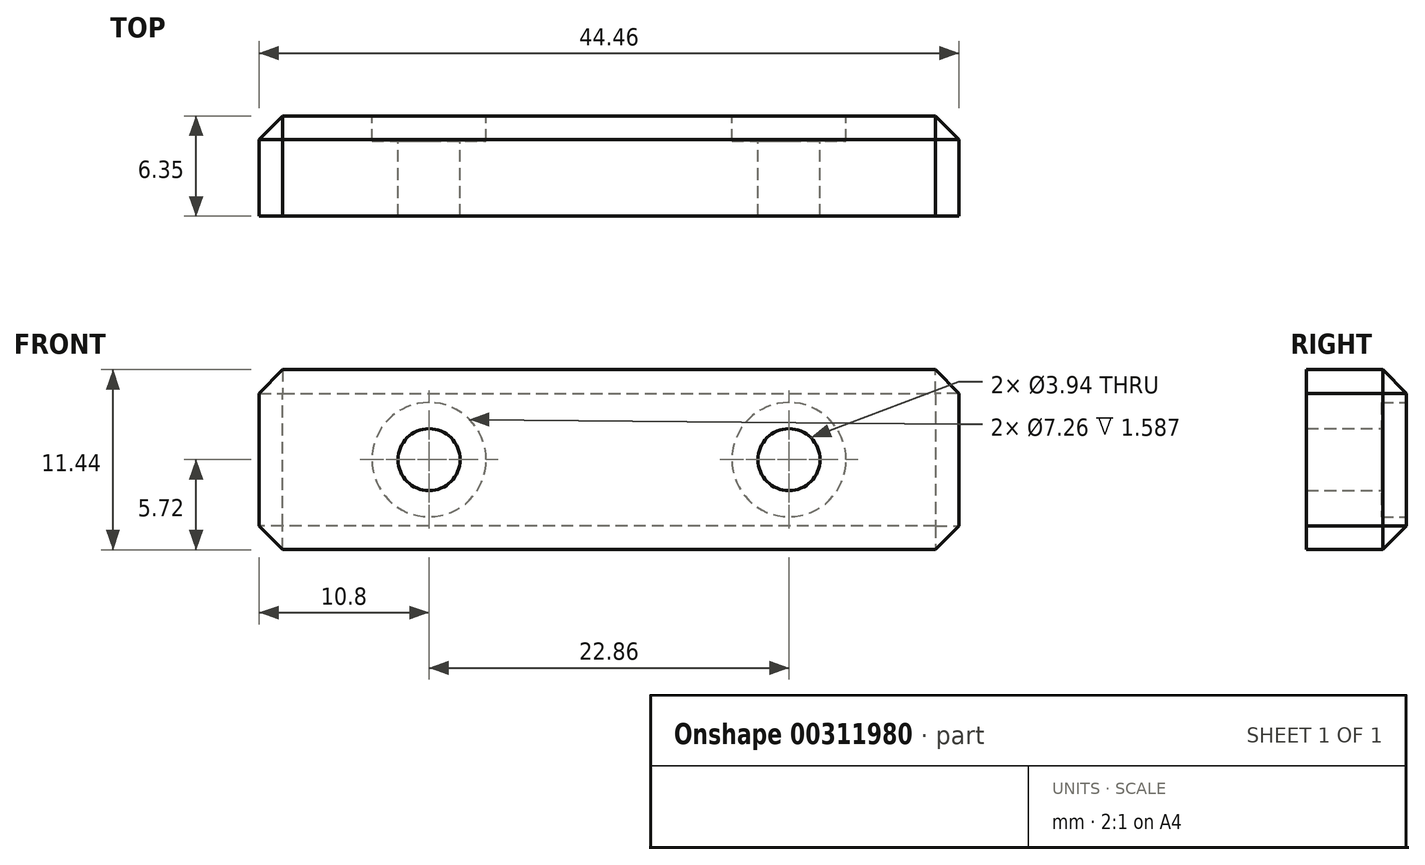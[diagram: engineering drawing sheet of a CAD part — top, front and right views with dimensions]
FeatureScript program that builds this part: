
annotation { "Feature Type Name" : "Feature", "Feature Type Description" : "" }
export const myFeature = defineFeature(function(context is Context, id is Id, definition is map)
    precondition{}
    {
        {
            var Q0;
            Q0=qCreatedBy(makeId("Front.planeOp"),FACE);
            var sketch = newSketch(context, id + "F0", { "sketchPlane" : qUnion([Q0])});
            skLineSegment(sketch, "E0.bottom", {"start": v(-22.23, 5.72) * mm, "end": v(22.23, 5.72) * mm});
            skLineSegment(sketch, "E0.top", {"start": v(-22.23, -5.71) * mm, "end": v(22.23, -5.71) * mm});
            skLineSegment(sketch, "E0.left", {"start": v(-22.23, 5.72) * mm, "end": v(-22.23, -5.71) * mm});
            skLineSegment(sketch, "E0.right", {"start": v(22.23, 5.72) * mm, "end": v(22.23, -5.71) * mm});
            skPoint(sketch, "E0.middle", {"position": v(0, 0) * mm});
            skPoint(sketch, "E1", {"position": v(-11.43, 0) * mm});
            skPoint(sketch, "E2", {"position": v(11.43, 0) * mm});
            skSolve(sketch);
        }
        {
            var Q0;
            Q0 = qSketchRegion(id + "F0", true);
            extrude(context, id + "F1", {"entities" : qUnion([Q0]), "depth" : 6.35 * mm});
        }
        {
            var Q0;
            Q0=sQuery(id+"F0.wireOp",VERTEX,"E1");
            var Q1;
            Q1=sQuery(id+"F0.wireOp",VERTEX,"E2");
            var Q2;
            Q2=makeQuery(id+"F1.opExtrude","SWEPT_BODY",BODY,{"disambiguationData":[OSD([sQuery(id+"F0.wireOp",EDGE,"E0.bottom"),sQuery(id+"F0.wireOp",EDGE,"E0.top"),sQuery(id+"F0.wireOp",EDGE,"E0.left"),sQuery(id+"F0.wireOp",EDGE,"E0.right")])]});
            hole(context, id + "F2", {"style" : HoleStyle.C_BORE, "endStyle" : HoleEndStyle.BLIND, "oppositeDirection" : true, "holeDiameter" : 3.94 * mm, "cBoreDiameter" : 7.26 * mm, "cBoreDepth" : 1.59 * mm, "holeDepth" : 6.35 * mm, "tappedDepth" : 12.7 * mm, "tapClearance" : 3, "locations" : qUnion([Q0, Q1]), "scope" : qUnion([Q2])});
        }
        {
            var Q0;
            Q0=makeQuery(id+"F1.opExtrude","CAP_EDGE",EDGE,{"disambiguationData":[OSD([sQuery(id+"F0.wireOp",EDGE,"E0.bottom")])],"isStart":true});
            var Q1;
            Q1=makeQuery(id+"F1.opExtrude","CAP_EDGE",EDGE,{"disambiguationData":[OSD([sQuery(id+"F0.wireOp",EDGE,"E0.top")])],"isStart":true});
            var Q2;
            Q2=makeQuery(id+"F1.opExtrude","CAP_EDGE",EDGE,{"disambiguationData":[OSD([sQuery(id+"F0.wireOp",EDGE,"E0.right")])],"isStart":true});
            var Q3;
            Q3=makeQuery(id+"F1.opExtrude","CAP_EDGE",EDGE,{"disambiguationData":[OSD([sQuery(id+"F0.wireOp",EDGE,"E0.left")])],"isStart":true});
            var Q4;
            Q4=makeQuery(id+"F1.opExtrude","SWEPT_EDGE",EDGE,{"disambiguationData":[OSD([sQuery(id+"F0.wireOp",EDGE,"E0.top"),sQuery(id+"F0.wireOp",EDGE,"E0.right")])]});
            var Q5;
            Q5=makeQuery(id+"F1.opExtrude","SWEPT_EDGE",EDGE,{"disambiguationData":[OSD([sQuery(id+"F0.wireOp",EDGE,"E0.bottom"),sQuery(id+"F0.wireOp",EDGE,"E0.right")])]});
            var Q6;
            Q6=makeQuery(id+"F1.opExtrude","SWEPT_EDGE",EDGE,{"disambiguationData":[OSD([sQuery(id+"F0.wireOp",EDGE,"E0.bottom"),sQuery(id+"F0.wireOp",EDGE,"E0.left")])]});
            var Q7;
            Q7=makeQuery(id+"F1.opExtrude","SWEPT_EDGE",EDGE,{"disambiguationData":[OSD([sQuery(id+"F0.wireOp",EDGE,"E0.top"),sQuery(id+"F0.wireOp",EDGE,"E0.left")])]});
            chamfer(context, id + "F3", {"entities" : qUnion([Q0, Q1, Q2, Q3, Q4, Q5, Q6, Q7]), "width" : 1.5 * mm, "tangentPropagation" : true});
        }
    });
